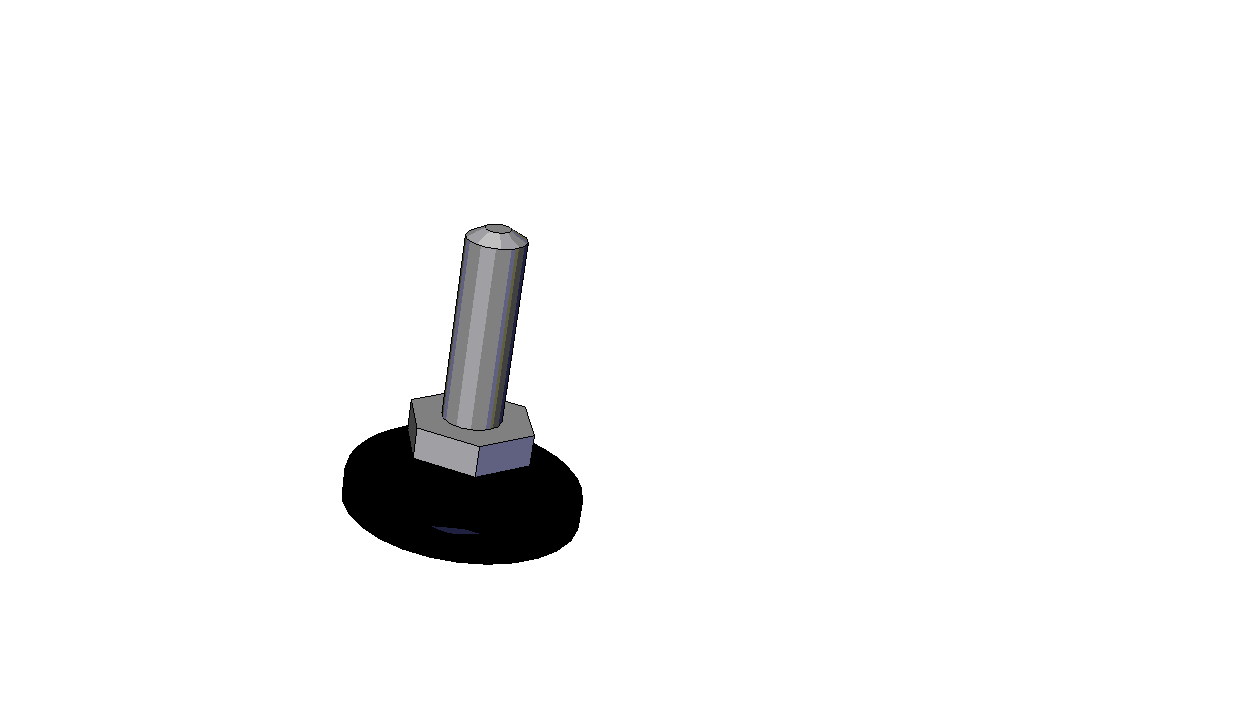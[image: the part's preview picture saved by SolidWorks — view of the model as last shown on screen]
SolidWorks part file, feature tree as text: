
SOLIDWORKS PART (.sldprt)
format: sldprt  version: not decoded by parser v0  size: 123,392 bytes
history: native  units: mm
features: plane x3, sketch x3, extrude x2, material x1, revolve x1, fillet x1, chamfer x1 (+8 scaffold rows collapsed)
feature tree (20):
  scaffold x8  (default folders/planes/origin — collapsed)
  material  "Matériau <non spécifié>"
  plane  "Plan1"
  plane  "Plan2"
  plane  "Plan3"
  sketch  "Esquisse1"  dims[D1=17.5mm]
  revolve  "Base-Révolution"  Angle=360deg
  sketch  "Esquisse2"
  extrude  "Boss.-Extru.1"  Depth=5mm
  sketch  "Esquisse3"  dims[D1=10.0mm]
  extrude  "Boss.-Extru.2"  Depth=30mm
  fillet  "Congé1"  Radius=2mm
  chamfer  "Chanfrein1"  Distance=1.5mm Angle=60deg
decode coverage: 7 of 8 modeling features carry decoded parameters
note: suppression state not decoded; provenance and decode notes live in map.json
